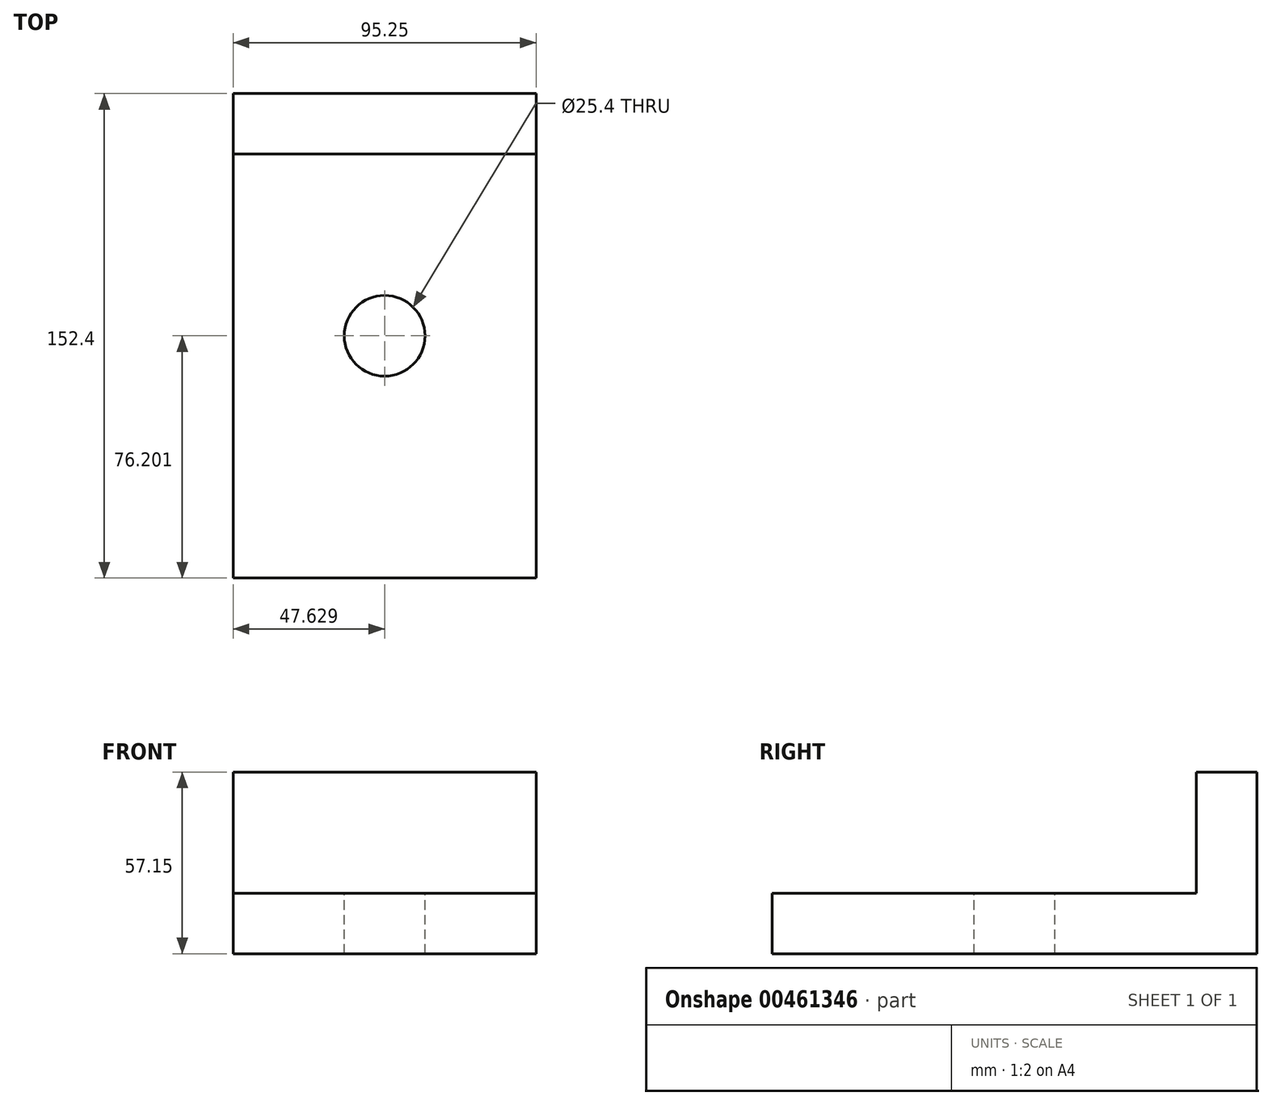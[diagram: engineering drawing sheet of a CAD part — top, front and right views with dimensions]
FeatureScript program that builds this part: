
annotation { "Feature Type Name" : "Feature", "Feature Type Description" : "" }
export const myFeature = defineFeature(function(context is Context, id is Id, definition is map)
    precondition{}
    {
        {
            var Q0;
            Q0=qCreatedBy(makeId("Top.planeOp"),FACE);
            var sketch = newSketch(context, id + "F0", { "sketchPlane" : qUnion([Q0])});
            skLineSegment(sketch, "E0.bottom", {"start": v(-68.36, 82.85) * mm, "end": v(26.9, 82.85) * mm});
            skLineSegment(sketch, "E0.top", {"start": v(-68.36, -69.55) * mm, "end": v(26.9, -69.55) * mm});
            skLineSegment(sketch, "E0.left", {"start": v(-68.36, 82.85) * mm, "end": v(-68.36, -69.55) * mm});
            skLineSegment(sketch, "E0.right", {"start": v(26.9, 82.85) * mm, "end": v(26.9, -69.55) * mm});
            skSolve(sketch);
        }
        {
            var Q0;
            Q0=makeQuery(id+"F0.imprint","IMPRINT",FACE,{"disambiguationData":[TD([[makeQuery(id+"F0.imprint","IMPRINT",EDGE,{"derivedFrom":sQuery(id+"F0.wireOp",EDGE,"E0.bottom")}),-1.0]])]});
            extrude(context, id + "F1", {"entities" : qUnion([Q0]), "depth" : 19.05 * mm});
        }
        {
            var Q0;
            Q0=makeQuery(id+"F1.opExtrude","CAP_FACE",FACE,{"disambiguationData":[OSD([sQuery(id+"F0.wireOp",EDGE,"E0.bottom"),sQuery(id+"F0.wireOp",EDGE,"E0.top"),sQuery(id+"F0.wireOp",EDGE,"E0.left"),sQuery(id+"F0.wireOp",EDGE,"E0.right")])],"isStart":false});
            var sketch = newSketch(context, id + "F2", { "sketchPlane" : qUnion([Q0])});
            skCircle(sketch, "E1", {"center": v(-20.73, 6.65) * mm, "radius": 12.7 * mm});
            skPoint(sketch, "E1.centerSnap0", {"position": v(-68.36, 6.65) * mm});
            skPoint(sketch, "E1.centerSnap1", {"position": v(-20.73, 82.85) * mm});
            skSolve(sketch);
        }
        {
            var Q0;
            Q0=makeQuery(id+"F2.imprint","IMPRINT",FACE,{"disambiguationData":[TD([[makeQuery(id+"F2.imprint","IMPRINT",EDGE,{"derivedFrom":sQuery(id+"F2.wireOp",EDGE,"E1")}),-1.0]])]});
            var sketch = newSketch(context, id + "F3", { "sketchPlane" : qUnion([Q0])});
            skLineSegment(sketch, "E2.bottom", {"start": v(-68.36, 82.85) * mm, "end": v(26.9, 82.85) * mm});
            skLineSegment(sketch, "E2.top", {"start": v(-68.36, 63.8) * mm, "end": v(26.9, 63.8) * mm});
            skLineSegment(sketch, "E2.left", {"start": v(-68.36, 82.85) * mm, "end": v(-68.36, 63.8) * mm});
            skLineSegment(sketch, "E2.right", {"start": v(26.9, 82.85) * mm, "end": v(26.9, 63.8) * mm});
            skSolve(sketch);
        }
        {
            var Q0;
            Q0 = qSketchRegion(id + "F3", true);
            extrude(context, id + "F4", {"entities" : qUnion([Q0]), "operationType" : NewBodyOperationType.ADD, "depth" : 38.1 * mm});
        }
        {
            var Q0;
            Q0=makeQuery(id+"F2.imprint","IMPRINT",FACE,{"disambiguationData":[TD([[makeQuery(id+"F2.imprint","IMPRINT",EDGE,{"derivedFrom":sQuery(id+"F2.wireOp",EDGE,"E1")}),1.0]])]});
            extrude(context, id + "F5", {"entities" : qUnion([Q0]), "operationType" : NewBodyOperationType.REMOVE, "endBound" : BoundingType.THROUGH_ALL, "oppositeDirection" : true, "depth" : 25.4 * mm});
        }
    });
